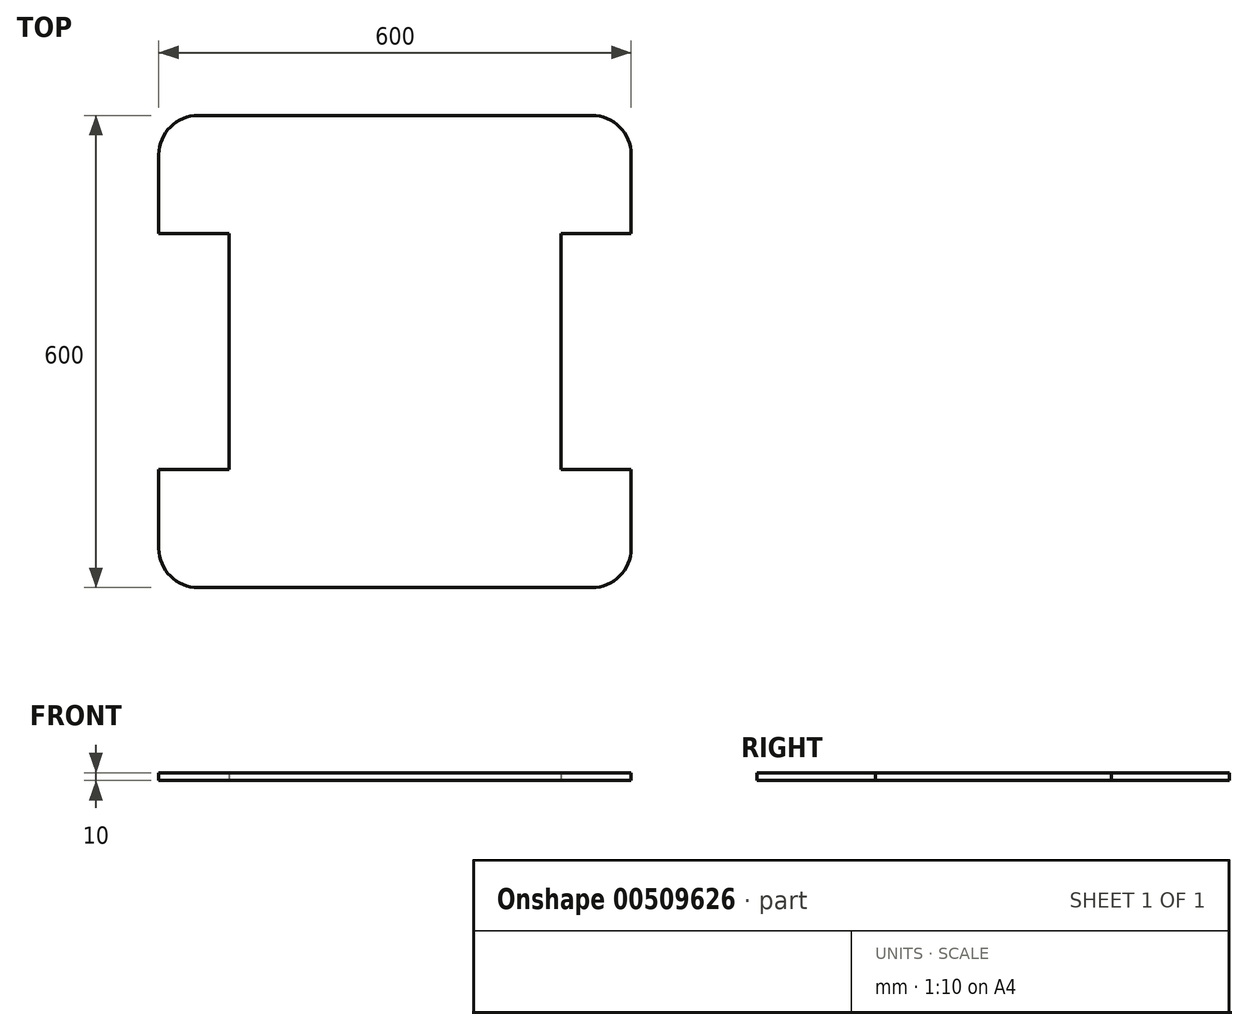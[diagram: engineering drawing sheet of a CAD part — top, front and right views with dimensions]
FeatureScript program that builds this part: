
annotation { "Feature Type Name" : "Feature", "Feature Type Description" : "" }
export const myFeature = defineFeature(function(context is Context, id is Id, definition is map)
    precondition{}
    {
        {
            var Q0;
            Q0=qCreatedBy(makeId("Top.planeOp"),FACE);
            var sketch = newSketch(context, id + "F0", { "sketchPlane" : qUnion([Q0])});
            skLineSegment(sketch, "E0.bottom", {"start": v(250, 300) * mm, "end": v(-250, 300) * mm});
            skLineSegment(sketch, "E0.top", {"start": v(250, -300) * mm, "end": v(-250, -300) * mm});
            skLineSegment(sketch, "E0.left", {"start": v(300, 250) * mm, "end": v(300, 150) * mm});
            skLineSegment(sketch, "E0.right", {"start": v(-300, 250) * mm, "end": v(-300, 150) * mm});
            skPoint(sketch, "E0.middle", {"position": v(0, 0) * mm});
            skPoint(sketch, "E1.visualSharp", {"position": v(-300, 300) * mm});
            skArc(sketch, "E1.filletArc", {"start": v(-250, 300) * mm, "mid": v(-285.36, 285.36) * mm, "end": v(-300, 250) * mm});
            skPoint(sketch, "E2.visualSharp", {"position": v(300, 300) * mm});
            skArc(sketch, "E2.filletArc", {"start": v(300, 250) * mm, "mid": v(285.36, 285.36) * mm, "end": v(250, 300) * mm});
            skPoint(sketch, "E3.visualSharp", {"position": v(300, -300) * mm});
            skArc(sketch, "E3.filletArc", {"start": v(250, -300) * mm, "mid": v(285.36, -285.36) * mm, "end": v(300, -250) * mm});
            skPoint(sketch, "E4.visualSharp", {"position": v(-300, -300) * mm});
            skArc(sketch, "E4.filletArc", {"start": v(-300, -250) * mm, "mid": v(-285.36, -285.36) * mm, "end": v(-250, -300) * mm});
            skLineSegment(sketch, "E5", {"start": v(-210.95, 150) * mm, "end": v(-300, 150) * mm});
            skLineSegment(sketch, "E6.MirrorCS", {"start": v(-210.95, -150) * mm, "end": v(-300, -150) * mm});
            skLineSegment(sketch, "E7", {"start": v(-210.95, 150) * mm, "end": v(-210.95, -150) * mm});
            skLineSegment(sketch, "E8.trimOffspring", {"start": v(-300, -150) * mm, "end": v(-300, -250) * mm});
            skLineSegment(sketch, "E9.MirrorCS", {"start": v(210.95, 150) * mm, "end": v(210.95, -150) * mm});
            skLineSegment(sketch, "E10.MirrorCS", {"start": v(210.95, 150) * mm, "end": v(300, 150) * mm});
            skLineSegment(sketch, "E11.MirrorCS", {"start": v(210.95, -150) * mm, "end": v(300, -150) * mm});
            skLineSegment(sketch, "E12.trimOffspring", {"start": v(300, -150) * mm, "end": v(300, -250) * mm});
            skSolve(sketch);
        }
        {
            var Q0;
            Q0=makeQuery(id+"F0.imprint","IMPRINT",FACE,{"disambiguationData":[TD([[makeQuery(id+"F0.imprint","IMPRINT",EDGE,{"derivedFrom":sQuery(id+"F0.wireOp",EDGE,"E0.bottom")}),1.0]])]});
            extrude(context, id + "F1", {"entities" : qUnion([Q0]), "depth" : 10 * mm});
        }
    });
